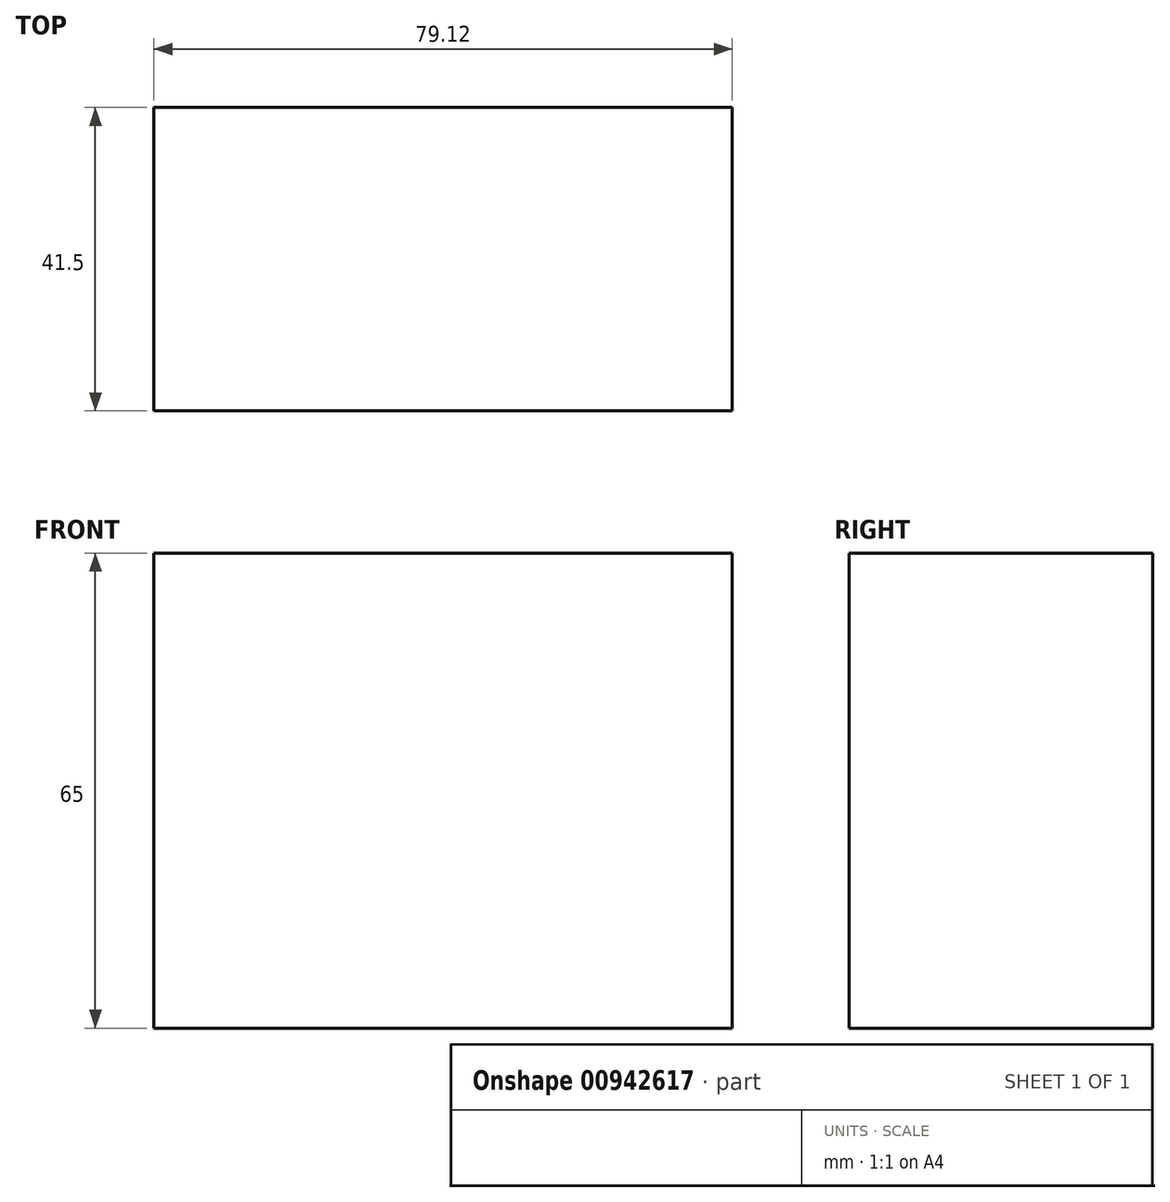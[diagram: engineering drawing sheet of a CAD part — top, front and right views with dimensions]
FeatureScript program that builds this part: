
annotation { "Feature Type Name" : "Feature", "Feature Type Description" : "" }
export const myFeature = defineFeature(function(context is Context, id is Id, definition is map)
    precondition{}
    {
        {
            var Q0;
            Q0=qCreatedBy(makeId("Front.planeOp"),FACE);
            var sketch = newSketch(context, id + "F0", { "sketchPlane" : qUnion([Q0])});
            skLineSegment(sketch, "E0.bottom", {"start": v(-50, 39.1) * mm, "end": v(29.12, 39.1) * mm});
            skLineSegment(sketch, "E0.top", {"start": v(-50, -25.9) * mm, "end": v(29.12, -25.9) * mm});
            skLineSegment(sketch, "E0.left", {"start": v(-50, 39.1) * mm, "end": v(-50, -25.9) * mm});
            skLineSegment(sketch, "E0.right", {"start": v(29.12, 39.1) * mm, "end": v(29.12, -25.9) * mm});
            skSolve(sketch);
        }
        {
            var Q0;
            Q0=makeQuery(id+"F0.imprint","IMPRINT",FACE,{"disambiguationData":[TD([[makeQuery(id+"F0.imprint","IMPRINT",EDGE,{"derivedFrom":sQuery(id+"F0.wireOp",EDGE,"E0.bottom")}),-1.0]])]});
            extrude(context, id + "F1", {"entities" : qUnion([Q0]), "depth" : 41.5 * mm, "offsetDistance" : 25 * mm});
        }
    });
